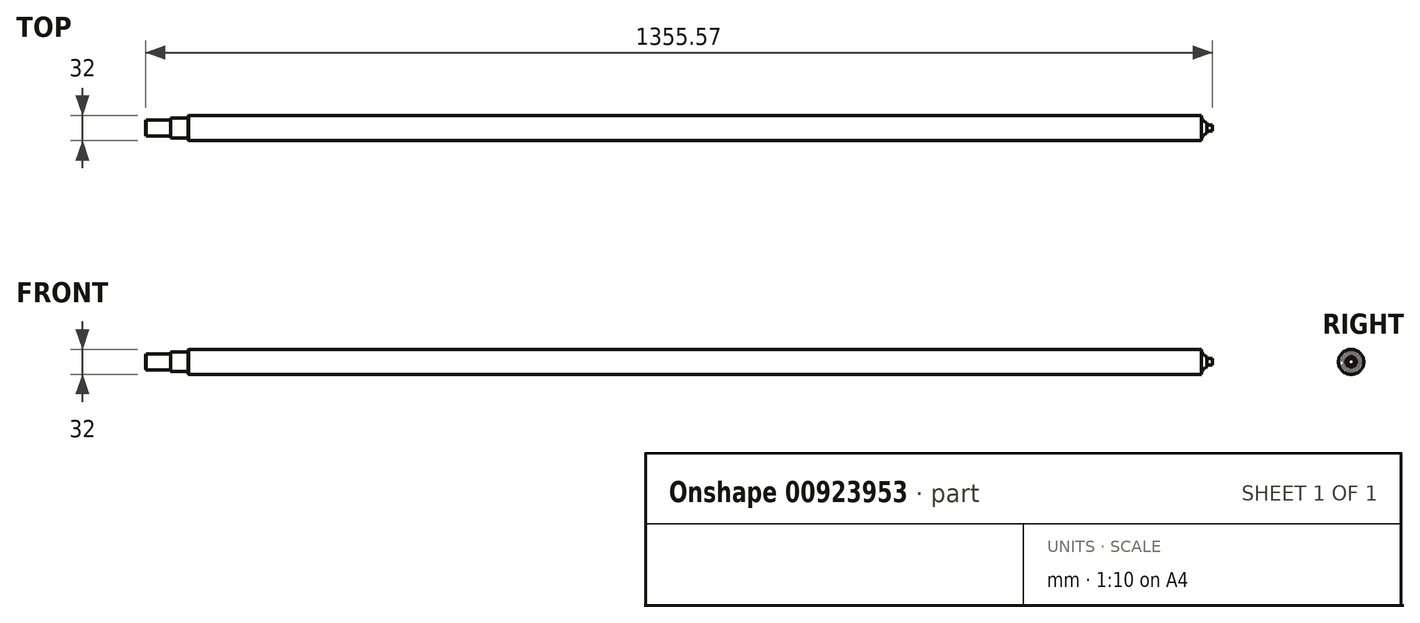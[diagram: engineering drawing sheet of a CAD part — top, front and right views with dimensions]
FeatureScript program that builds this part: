
annotation { "Feature Type Name" : "Feature", "Feature Type Description" : "" }
export const myFeature = defineFeature(function(context is Context, id is Id, definition is map)
    precondition{}
    {
        {
            var Q0;
            Q0=qCreatedBy(makeId("Front.planeOp"),FACE);
            var sketch = newSketch(context, id + "F0", { "sketchPlane" : qUnion([Q0])});
            skLineSegment(sketch, "E0", {"start": v(-39.63, 49.41) * mm, "end": v(1315.94, 49.41) * mm});
            skLineSegment(sketch, "E1", {"start": v(1315.94, 49.41) * mm, "end": v(1315.94, 53.41) * mm});
            skLineSegment(sketch, "E2", {"start": v(1315.94, 53.41) * mm, "end": v(1308.94, 53.41) * mm});
            skLineSegment(sketch, "E3", {"start": v(1308.94, 53.41) * mm, "end": v(1308.94, 55.98) * mm});
            skLineSegment(sketch, "E4", {"start": v(1301.78, 65.41) * mm, "end": v(14.37, 65.41) * mm});
            skLineSegment(sketch, "E5", {"start": v(14.37, 65.41) * mm, "end": v(14.37, 61.91) * mm});
            skLineSegment(sketch, "E6", {"start": v(14.37, 61.91) * mm, "end": v(-7.63, 61.91) * mm});
            skLineSegment(sketch, "E7", {"start": v(-7.63, 61.91) * mm, "end": v(-7.63, 59.41) * mm});
            skLineSegment(sketch, "E8", {"start": v(-7.63, 59.41) * mm, "end": v(-39.63, 59.41) * mm});
            skLineSegment(sketch, "E9", {"start": v(-39.63, 59.41) * mm, "end": v(-39.63, 49.41) * mm});
            skArc(sketch, "E10", {"start": v(1301.78, 65.41) * mm, "mid": v(1303.81, 59.52) * mm, "end": v(1308.94, 55.98) * mm});
            skSolve(sketch);
        }
        {
            var Q0;
            Q0=makeQuery(id+"F0.imprint","IMPRINT",FACE,{"disambiguationData":[TD([[makeQuery(id+"F0.imprint","IMPRINT",EDGE,{"derivedFrom":sQuery(id+"F0.wireOp",EDGE,"E0")}),1.0]])]});
            var Q1;
            Q1=sQuery(id+"F0.wireOp",EDGE,"E0");
            revolve(context, id + "F1", {"surfaceOperationType" : NewSurfaceOperationType.NEW, "entities" : qUnion([Q0]), "axis" : qUnion([Q1]), "revolveType" : RevolveType.FULL});
        }
        {
            var Q0;
            Q0=makeQuery(id+"F1.opRevolve","SWEPT_EDGE",EDGE,{"disambiguationData":[OSD([sQuery(id+"F0.wireOp",EDGE,"E4"),sQuery(id+"F0.wireOp",EDGE,"E5")])]});
            chamfer(context, id + "F2", {"entities" : qUnion([Q0]), "width" : 1 * mm, "tangentPropagation" : true});
        }
        {
            var Q0;
            Q0=makeQuery(id+"F1.opRevolve","SWEPT_EDGE",EDGE,{"disambiguationData":[OSD([sQuery(id+"F0.wireOp",EDGE,"E6"),sQuery(id+"F0.wireOp",EDGE,"E7")])]});
            chamfer(context, id + "F3", {"entities" : qUnion([Q0]), "width" : .25 * mm, "tangentPropagation" : true});
        }
        {
            var Q0;
            Q0=makeQuery(id+"F1.opRevolve","SWEPT_EDGE",EDGE,{"disambiguationData":[OSD([sQuery(id+"F0.wireOp",EDGE,"E8"),sQuery(id+"F0.wireOp",EDGE,"E9")])]});
            chamfer(context, id + "F4", {"entities" : qUnion([Q0]), "width" : 1 * mm, "tangentPropagation" : true});
        }
    });
